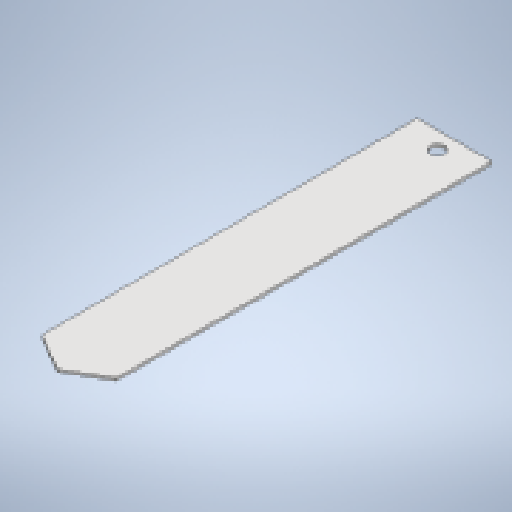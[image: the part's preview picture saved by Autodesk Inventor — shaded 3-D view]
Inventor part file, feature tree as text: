
AUTODESK INVENTOR PART (.ipt)
format: ipt  version: 2025.4 (Build 294407000, 407)  size: 169,984 bytes
history: native  units: mm
features: other x2, sheet_metal_op x1, sketch x1
ambient origin geometry x8: Origin, YZ Plane, XZ Plane, XY Plane, X Axis, Y Axis, Z Axis, Center Point
bodies: Body1 (feature_tree)
feature tree (4):
  sheet_metal_op  "Face2"
  sketch  "Sketch6"  dims[d40=120.0deg d42=86.0mm d43=17.0mm d44=880.0mm d45=920.0mm d46=3.0mm]
  other  "Plate3"
  other  "Definition1"
